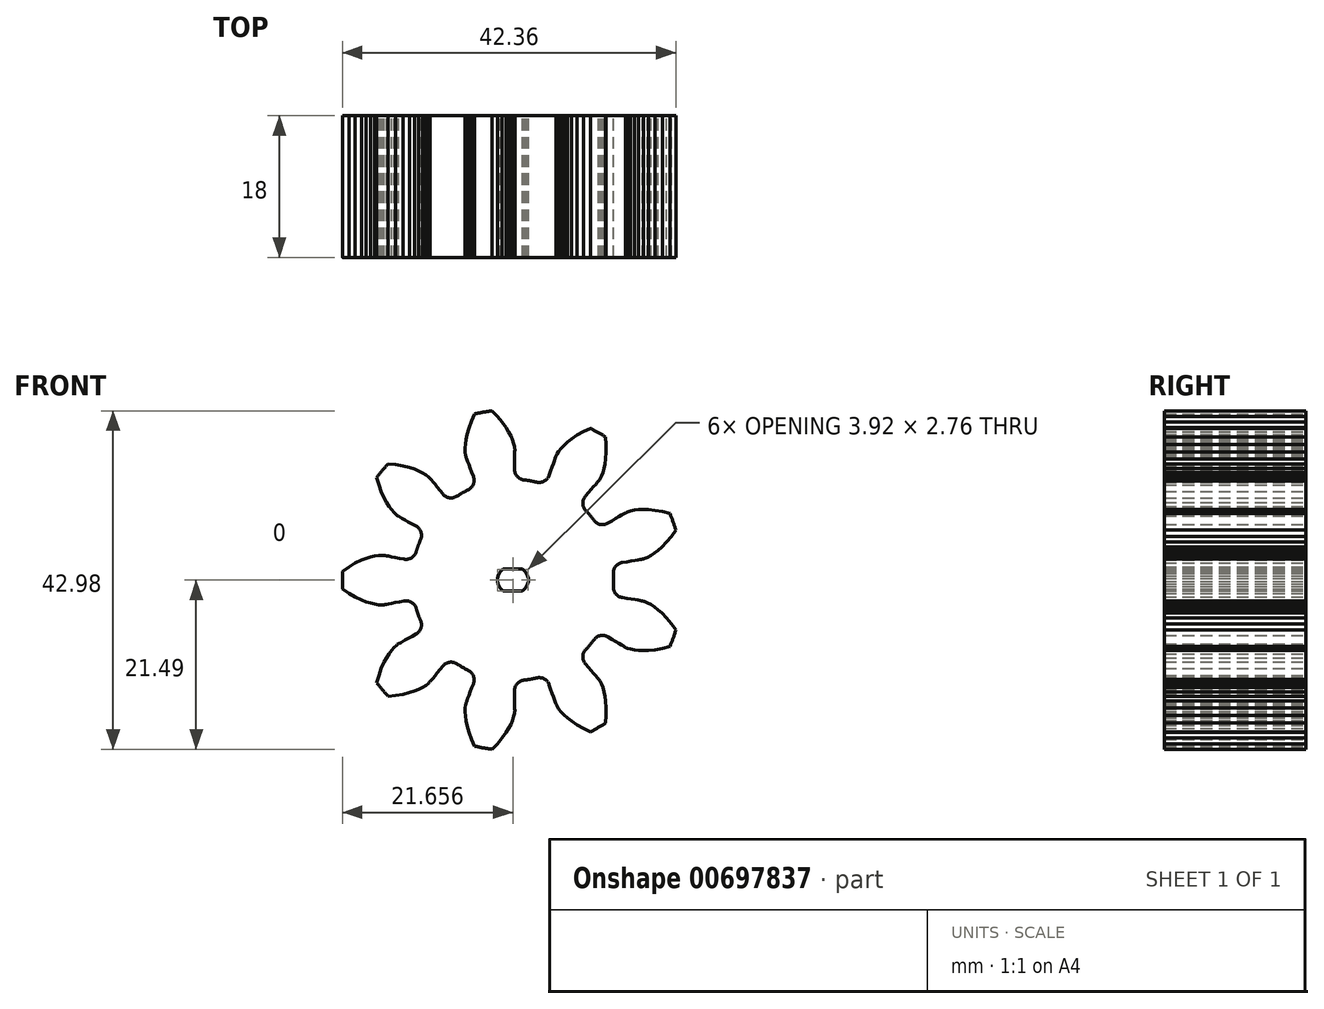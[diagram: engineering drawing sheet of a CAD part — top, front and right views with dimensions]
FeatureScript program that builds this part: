
annotation { "Feature Type Name" : "Feature", "Feature Type Description" : "" }
export const myFeature = defineFeature(function(context is Context, id is Id, definition is map)
    precondition{}
    {
        {
            var Q0;
            Q0=qCreatedBy(makeId("Front.planeOp"),FACE);
            var sketch = newSketch(context, id + "F0", { "sketchPlane" : qUnion([Q0])});
            skLineSegment(sketch, "E0", {"start": v(1.7, -1.38) * mm, "end": v(1.98, -1.13) * mm});
            skLineSegment(sketch, "E1", {"start": v(1.98, -1.13) * mm, "end": v(2.2, -0.84) * mm});
            skLineSegment(sketch, "E2", {"start": v(2.2, -0.84) * mm, "end": v(2.36, -0.52) * mm});
            skLineSegment(sketch, "E3", {"start": v(2.36, -0.52) * mm, "end": v(2.43, -0.18) * mm});
            skLineSegment(sketch, "E4", {"start": v(2.43, -0.18) * mm, "end": v(2.43, 0.18) * mm});
            skLineSegment(sketch, "E5", {"start": v(2.43, 0.18) * mm, "end": v(2.36, 0.52) * mm});
            skLineSegment(sketch, "E6", {"start": v(2.36, 0.52) * mm, "end": v(2.2, 0.84) * mm});
            skLineSegment(sketch, "E7", {"start": v(2.2, 0.84) * mm, "end": v(1.98, 1.13) * mm});
            skLineSegment(sketch, "E8", {"start": v(1.98, 1.13) * mm, "end": v(1.7, 1.38) * mm});
            skLineSegment(sketch, "E9", {"start": v(1.7, 1.38) * mm, "end": v(-0.75, 1.38) * mm});
            skLineSegment(sketch, "E10", {"start": v(-0.75, 1.38) * mm, "end": v(-1.03, 1.13) * mm});
            skLineSegment(sketch, "E11", {"start": v(-1.03, 1.13) * mm, "end": v(-1.25, 0.84) * mm});
            skLineSegment(sketch, "E12", {"start": v(-1.25, 0.84) * mm, "end": v(-1.4, 0.52) * mm});
            skLineSegment(sketch, "E13", {"start": v(-1.4, 0.52) * mm, "end": v(-1.48, 0.18) * mm});
            skLineSegment(sketch, "E14", {"start": v(-1.48, 0.18) * mm, "end": v(-1.48, -0.18) * mm});
            skLineSegment(sketch, "E15", {"start": v(-1.48, -0.18) * mm, "end": v(-1.4, -0.52) * mm});
            skLineSegment(sketch, "E16", {"start": v(-1.4, -0.52) * mm, "end": v(-1.25, -0.84) * mm});
            skLineSegment(sketch, "E17", {"start": v(-1.25, -0.84) * mm, "end": v(-1.03, -1.13) * mm});
            skLineSegment(sketch, "E18", {"start": v(-1.03, -1.13) * mm, "end": v(-0.75, -1.38) * mm});
            skLineSegment(sketch, "E19", {"start": v(1.7, -1.38) * mm, "end": v(-0.75, -1.38) * mm});
            skArc(sketch, "E20", {"start": v(20.42, -8.44) * mm, "mid": v(20.82, -7.4) * mm, "end": v(21.18, -6.35) * mm});
            skLineSegment(sketch, "E21", {"start": v(12.57, -7.23) * mm, "end": v(13.07, -7.53) * mm});
            skLineSegment(sketch, "E22", {"start": v(13.07, -7.53) * mm, "end": v(13.53, -7.8) * mm});
            skLineSegment(sketch, "E23", {"start": v(13.53, -7.8) * mm, "end": v(13.95, -8.05) * mm});
            skLineSegment(sketch, "E24", {"start": v(13.95, -8.05) * mm, "end": v(14.3, -8.26) * mm});
            skLineSegment(sketch, "E25", {"start": v(14.3, -8.26) * mm, "end": v(14.51, -8.39) * mm});
            skLineSegment(sketch, "E26", {"start": v(14.51, -8.39) * mm, "end": v(14.68, -8.48) * mm});
            skLineSegment(sketch, "E27", {"start": v(14.68, -8.48) * mm, "end": v(14.78, -8.54) * mm});
            skLineSegment(sketch, "E28", {"start": v(14.78, -8.54) * mm, "end": v(14.83, -8.57) * mm});
            skLineSegment(sketch, "E29", {"start": v(14.83, -8.57) * mm, "end": v(14.92, -8.6) * mm});
            skLineSegment(sketch, "E30", {"start": v(14.92, -8.6) * mm, "end": v(15.04, -8.66) * mm});
            skLineSegment(sketch, "E31", {"start": v(15.04, -8.66) * mm, "end": v(15.44, -8.78) * mm});
            skLineSegment(sketch, "E32", {"start": v(15.44, -8.78) * mm, "end": v(15.92, -8.87) * mm});
            skLineSegment(sketch, "E33", {"start": v(15.92, -8.87) * mm, "end": v(16.46, -8.94) * mm});
            skLineSegment(sketch, "E34", {"start": v(16.46, -8.94) * mm, "end": v(17.05, -8.96) * mm});
            skLineSegment(sketch, "E35", {"start": v(17.05, -8.96) * mm, "end": v(17.68, -8.95) * mm});
            skLineSegment(sketch, "E36", {"start": v(17.68, -8.95) * mm, "end": v(18.55, -8.86) * mm});
            skLineSegment(sketch, "E37", {"start": v(18.55, -8.86) * mm, "end": v(19.47, -8.7) * mm});
            skLineSegment(sketch, "E38", {"start": v(19.47, -8.7) * mm, "end": v(20.42, -8.44) * mm});
            skArc(sketch, "E39", {"start": v(10.78, -7.59) * mm, "mid": v(11.6, -7.06) * mm, "end": v(12.57, -7.23) * mm});
            skArc(sketch, "E40", {"start": v(9.74, -8.83) * mm, "mid": v(10.28, -8.22) * mm, "end": v(10.78, -7.59) * mm});
            skArc(sketch, "E41", {"start": v(9.7, -10.65) * mm, "mid": v(9.36, -9.73) * mm, "end": v(9.74, -8.83) * mm});
            skLineSegment(sketch, "E42", {"start": v(9.7, -10.65) * mm, "end": v(10.08, -11.1) * mm});
            skLineSegment(sketch, "E43", {"start": v(10.08, -11.1) * mm, "end": v(10.43, -11.5) * mm});
            skLineSegment(sketch, "E44", {"start": v(10.43, -11.5) * mm, "end": v(10.75, -11.87) * mm});
            skLineSegment(sketch, "E45", {"start": v(10.75, -11.87) * mm, "end": v(11, -12.17) * mm});
            skLineSegment(sketch, "E46", {"start": v(11, -12.17) * mm, "end": v(11.17, -12.36) * mm});
            skLineSegment(sketch, "E47", {"start": v(11.17, -12.36) * mm, "end": v(11.3, -12.51) * mm});
            skLineSegment(sketch, "E48", {"start": v(11.3, -12.51) * mm, "end": v(11.37, -12.6) * mm});
            skLineSegment(sketch, "E49", {"start": v(11.37, -12.6) * mm, "end": v(11.4, -12.64) * mm});
            skLineSegment(sketch, "E50", {"start": v(11.4, -12.64) * mm, "end": v(11.46, -12.73) * mm});
            skLineSegment(sketch, "E51", {"start": v(11.46, -12.73) * mm, "end": v(11.53, -12.84) * mm});
            skLineSegment(sketch, "E52", {"start": v(11.53, -12.84) * mm, "end": v(11.72, -13.21) * mm});
            skLineSegment(sketch, "E53", {"start": v(11.72, -13.21) * mm, "end": v(11.9, -13.66) * mm});
            skLineSegment(sketch, "E54", {"start": v(11.9, -13.66) * mm, "end": v(12.05, -14.19) * mm});
            skLineSegment(sketch, "E55", {"start": v(12.05, -14.19) * mm, "end": v(12.18, -14.76) * mm});
            skLineSegment(sketch, "E56", {"start": v(12.18, -14.76) * mm, "end": v(12.28, -15.38) * mm});
            skLineSegment(sketch, "E57", {"start": v(12.28, -15.38) * mm, "end": v(12.34, -16.26) * mm});
            skLineSegment(sketch, "E58", {"start": v(12.34, -16.26) * mm, "end": v(12.33, -17.2) * mm});
            skLineSegment(sketch, "E59", {"start": v(12.33, -17.2) * mm, "end": v(12.25, -18.17) * mm});
            skArc(sketch, "E60", {"start": v(10.32, -19.28) * mm, "mid": v(11.3, -18.75) * mm, "end": v(12.25, -18.17) * mm});
            skLineSegment(sketch, "E61", {"start": v(5.1, -13.31) * mm, "end": v(5.29, -13.86) * mm});
            skLineSegment(sketch, "E62", {"start": v(5.29, -13.86) * mm, "end": v(5.46, -14.37) * mm});
            skLineSegment(sketch, "E63", {"start": v(5.46, -14.37) * mm, "end": v(5.62, -14.83) * mm});
            skLineSegment(sketch, "E64", {"start": v(5.62, -14.83) * mm, "end": v(5.75, -15.2) * mm});
            skLineSegment(sketch, "E65", {"start": v(5.75, -15.2) * mm, "end": v(5.84, -15.45) * mm});
            skLineSegment(sketch, "E66", {"start": v(5.84, -15.45) * mm, "end": v(5.9, -15.63) * mm});
            skLineSegment(sketch, "E67", {"start": v(5.9, -15.63) * mm, "end": v(5.94, -15.74) * mm});
            skLineSegment(sketch, "E68", {"start": v(5.94, -15.74) * mm, "end": v(5.96, -15.79) * mm});
            skLineSegment(sketch, "E69", {"start": v(5.96, -15.79) * mm, "end": v(6, -15.88) * mm});
            skLineSegment(sketch, "E70", {"start": v(6, -15.88) * mm, "end": v(6.07, -16) * mm});
            skLineSegment(sketch, "E71", {"start": v(6.07, -16) * mm, "end": v(6.3, -16.34) * mm});
            skLineSegment(sketch, "E72", {"start": v(6.3, -16.34) * mm, "end": v(6.6, -16.72) * mm});
            skLineSegment(sketch, "E73", {"start": v(6.6, -16.72) * mm, "end": v(6.97, -17.12) * mm});
            skLineSegment(sketch, "E74", {"start": v(6.97, -17.12) * mm, "end": v(7.4, -17.52) * mm});
            skLineSegment(sketch, "E75", {"start": v(7.4, -17.52) * mm, "end": v(7.9, -17.91) * mm});
            skLineSegment(sketch, "E76", {"start": v(7.9, -17.91) * mm, "end": v(8.63, -18.4) * mm});
            skLineSegment(sketch, "E77", {"start": v(8.63, -18.4) * mm, "end": v(9.44, -18.87) * mm});
            skLineSegment(sketch, "E78", {"start": v(9.44, -18.87) * mm, "end": v(10.32, -19.28) * mm});
            skArc(sketch, "E79", {"start": v(3.5, -12.43) * mm, "mid": v(4.46, -12.56) * mm, "end": v(5.1, -13.31) * mm});
            skArc(sketch, "E80", {"start": v(1.9, -12.72) * mm, "mid": v(2.7, -12.6) * mm, "end": v(3.5, -12.43) * mm});
            skArc(sketch, "E81", {"start": v(0.69, -14.09) * mm, "mid": v(1.03, -13.17) * mm, "end": v(1.9, -12.72) * mm});
            skLineSegment(sketch, "E82", {"start": v(0.69, -14.09) * mm, "end": v(0.7, -14.67) * mm});
            skLineSegment(sketch, "E83", {"start": v(0.7, -14.67) * mm, "end": v(0.7, -15.21) * mm});
            skLineSegment(sketch, "E84", {"start": v(0.7, -15.21) * mm, "end": v(0.71, -15.7) * mm});
            skLineSegment(sketch, "E85", {"start": v(0.71, -15.7) * mm, "end": v(0.72, -16.1) * mm});
            skLineSegment(sketch, "E86", {"start": v(0.72, -16.1) * mm, "end": v(0.72, -16.35) * mm});
            skLineSegment(sketch, "E87", {"start": v(0.72, -16.35) * mm, "end": v(0.72, -16.54) * mm});
            skLineSegment(sketch, "E88", {"start": v(0.72, -16.54) * mm, "end": v(0.72, -16.66) * mm});
            skLineSegment(sketch, "E89", {"start": v(0.72, -16.66) * mm, "end": v(0.72, -16.71) * mm});
            skLineSegment(sketch, "E90", {"start": v(0.72, -16.71) * mm, "end": v(0.71, -16.81) * mm});
            skLineSegment(sketch, "E91", {"start": v(0.71, -16.81) * mm, "end": v(0.7, -16.95) * mm});
            skLineSegment(sketch, "E92", {"start": v(0.7, -16.95) * mm, "end": v(0.6, -17.35) * mm});
            skLineSegment(sketch, "E93", {"start": v(0.6, -17.35) * mm, "end": v(0.44, -17.8) * mm});
            skLineSegment(sketch, "E94", {"start": v(0.44, -17.8) * mm, "end": v(0.23, -18.3) * mm});
            skLineSegment(sketch, "E95", {"start": v(0.23, -18.3) * mm, "end": v(-0.05, -18.83) * mm});
            skLineSegment(sketch, "E96", {"start": v(-0.05, -18.83) * mm, "end": v(-0.37, -19.37) * mm});
            skLineSegment(sketch, "E97", {"start": v(-0.37, -19.37) * mm, "end": v(-0.89, -20.08) * mm});
            skLineSegment(sketch, "E98", {"start": v(-0.89, -20.08) * mm, "end": v(-1.5, -20.8) * mm});
            skLineSegment(sketch, "E99", {"start": v(-1.5, -20.8) * mm, "end": v(-2.18, -21.49) * mm});
            skArc(sketch, "E100", {"start": v(-4.37, -21.1) * mm, "mid": v(-3.28, -21.32) * mm, "end": v(-2.18, -21.49) * mm});
            skLineSegment(sketch, "E101", {"start": v(-4.54, -13.16) * mm, "end": v(-4.75, -13.71) * mm});
            skLineSegment(sketch, "E102", {"start": v(-4.75, -13.71) * mm, "end": v(-4.94, -14.22) * mm});
            skLineSegment(sketch, "E103", {"start": v(-4.94, -14.22) * mm, "end": v(-5.11, -14.66) * mm});
            skLineSegment(sketch, "E104", {"start": v(-5.11, -14.66) * mm, "end": v(-5.26, -15.04) * mm});
            skLineSegment(sketch, "E105", {"start": v(-5.26, -15.04) * mm, "end": v(-5.35, -15.28) * mm});
            skLineSegment(sketch, "E106", {"start": v(-5.35, -15.28) * mm, "end": v(-5.41, -15.46) * mm});
            skLineSegment(sketch, "E107", {"start": v(-5.41, -15.46) * mm, "end": v(-5.45, -15.57) * mm});
            skLineSegment(sketch, "E108", {"start": v(-5.45, -15.57) * mm, "end": v(-5.47, -15.62) * mm});
            skLineSegment(sketch, "E109", {"start": v(-5.47, -15.62) * mm, "end": v(-5.5, -15.72) * mm});
            skLineSegment(sketch, "E110", {"start": v(-5.5, -15.72) * mm, "end": v(-5.52, -15.85) * mm});
            skLineSegment(sketch, "E111", {"start": v(-5.52, -15.85) * mm, "end": v(-5.57, -16.26) * mm});
            skLineSegment(sketch, "E112", {"start": v(-5.57, -16.26) * mm, "end": v(-5.58, -16.75) * mm});
            skLineSegment(sketch, "E113", {"start": v(-5.58, -16.75) * mm, "end": v(-5.55, -17.29) * mm});
            skLineSegment(sketch, "E114", {"start": v(-5.55, -17.29) * mm, "end": v(-5.48, -17.87) * mm});
            skLineSegment(sketch, "E115", {"start": v(-5.48, -17.87) * mm, "end": v(-5.35, -18.5) * mm});
            skLineSegment(sketch, "E116", {"start": v(-5.35, -18.5) * mm, "end": v(-5.11, -19.34) * mm});
            skLineSegment(sketch, "E117", {"start": v(-5.11, -19.34) * mm, "end": v(-4.79, -20.21) * mm});
            skLineSegment(sketch, "E118", {"start": v(-4.79, -20.21) * mm, "end": v(-4.37, -21.1) * mm});
            skArc(sketch, "E119", {"start": v(-5.2, -11.46) * mm, "mid": v(-4.55, -12.19) * mm, "end": v(-4.54, -13.16) * mm});
            skArc(sketch, "E120", {"start": v(-6.61, -10.65) * mm, "mid": v(-5.92, -11.08) * mm, "end": v(-5.2, -11.46) * mm});
            skArc(sketch, "E121", {"start": v(-8.42, -10.93) * mm, "mid": v(-7.57, -10.44) * mm, "end": v(-6.61, -10.65) * mm});
            skLineSegment(sketch, "E122", {"start": v(-8.42, -10.93) * mm, "end": v(-8.78, -11.38) * mm});
            skLineSegment(sketch, "E123", {"start": v(-8.78, -11.38) * mm, "end": v(-9.12, -11.8) * mm});
            skLineSegment(sketch, "E124", {"start": v(-9.12, -11.8) * mm, "end": v(-9.43, -12.17) * mm});
            skLineSegment(sketch, "E125", {"start": v(-9.43, -12.17) * mm, "end": v(-9.68, -12.49) * mm});
            skLineSegment(sketch, "E126", {"start": v(-9.68, -12.49) * mm, "end": v(-9.84, -12.68) * mm});
            skLineSegment(sketch, "E127", {"start": v(-9.84, -12.68) * mm, "end": v(-9.96, -12.83) * mm});
            skLineSegment(sketch, "E128", {"start": v(-9.96, -12.83) * mm, "end": v(-10.04, -12.92) * mm});
            skLineSegment(sketch, "E129", {"start": v(-10.04, -12.92) * mm, "end": v(-10.08, -12.96) * mm});
            skLineSegment(sketch, "E130", {"start": v(-10.08, -12.96) * mm, "end": v(-10.15, -13.03) * mm});
            skLineSegment(sketch, "E131", {"start": v(-10.15, -13.03) * mm, "end": v(-10.25, -13.12) * mm});
            skLineSegment(sketch, "E132", {"start": v(-10.25, -13.12) * mm, "end": v(-10.58, -13.37) * mm});
            skLineSegment(sketch, "E133", {"start": v(-10.58, -13.37) * mm, "end": v(-11, -13.62) * mm});
            skLineSegment(sketch, "E134", {"start": v(-11, -13.62) * mm, "end": v(-11.48, -13.87) * mm});
            skLineSegment(sketch, "E135", {"start": v(-11.48, -13.87) * mm, "end": v(-12.03, -14.1) * mm});
            skLineSegment(sketch, "E136", {"start": v(-12.03, -14.1) * mm, "end": v(-12.63, -14.3) * mm});
            skLineSegment(sketch, "E137", {"start": v(-12.63, -14.3) * mm, "end": v(-13.48, -14.5) * mm});
            skLineSegment(sketch, "E138", {"start": v(-13.48, -14.5) * mm, "end": v(-14.4, -14.66) * mm});
            skLineSegment(sketch, "E139", {"start": v(-14.4, -14.66) * mm, "end": v(-15.37, -14.75) * mm});
            skArc(sketch, "E140", {"start": v(-16.8, -13.05) * mm, "mid": v(-16.11, -13.92) * mm, "end": v(-15.37, -14.75) * mm});
            skLineSegment(sketch, "E141", {"start": v(-11.83, -6.86) * mm, "end": v(-12.34, -7.14) * mm});
            skLineSegment(sketch, "E142", {"start": v(-12.34, -7.14) * mm, "end": v(-12.81, -7.4) * mm});
            skLineSegment(sketch, "E143", {"start": v(-12.81, -7.4) * mm, "end": v(-13.23, -7.64) * mm});
            skLineSegment(sketch, "E144", {"start": v(-13.23, -7.64) * mm, "end": v(-13.58, -7.84) * mm});
            skLineSegment(sketch, "E145", {"start": v(-13.58, -7.84) * mm, "end": v(-13.8, -7.96) * mm});
            skLineSegment(sketch, "E146", {"start": v(-13.8, -7.96) * mm, "end": v(-13.97, -8.05) * mm});
            skLineSegment(sketch, "E147", {"start": v(-13.97, -8.05) * mm, "end": v(-14.08, -8.11) * mm});
            skLineSegment(sketch, "E148", {"start": v(-14.08, -8.11) * mm, "end": v(-14.12, -8.14) * mm});
            skLineSegment(sketch, "E149", {"start": v(-14.12, -8.14) * mm, "end": v(-14.2, -8.2) * mm});
            skLineSegment(sketch, "E150", {"start": v(-14.2, -8.2) * mm, "end": v(-14.3, -8.29) * mm});
            skLineSegment(sketch, "E151", {"start": v(-14.3, -8.29) * mm, "end": v(-14.6, -8.57) * mm});
            skLineSegment(sketch, "E152", {"start": v(-14.6, -8.57) * mm, "end": v(-14.93, -8.93) * mm});
            skLineSegment(sketch, "E153", {"start": v(-14.93, -8.93) * mm, "end": v(-15.26, -9.37) * mm});
            skLineSegment(sketch, "E154", {"start": v(-15.26, -9.37) * mm, "end": v(-15.57, -9.87) * mm});
            skLineSegment(sketch, "E155", {"start": v(-15.57, -9.87) * mm, "end": v(-15.87, -10.42) * mm});
            skLineSegment(sketch, "E156", {"start": v(-15.87, -10.42) * mm, "end": v(-16.23, -11.22) * mm});
            skLineSegment(sketch, "E157", {"start": v(-16.23, -11.22) * mm, "end": v(-16.55, -12.1) * mm});
            skLineSegment(sketch, "E158", {"start": v(-16.55, -12.1) * mm, "end": v(-16.8, -13.05) * mm});
            skArc(sketch, "E159", {"start": v(-11.25, -5.13) * mm, "mid": v(-11.2, -6.1) * mm, "end": v(-11.83, -6.86) * mm});
            skArc(sketch, "E160", {"start": v(-11.8, -3.6) * mm, "mid": v(-11.55, -4.38) * mm, "end": v(-11.25, -5.13) * mm});
            skArc(sketch, "E161", {"start": v(-13.36, -2.66) * mm, "mid": v(-12.4, -2.83) * mm, "end": v(-11.8, -3.6) * mm});
            skLineSegment(sketch, "E162", {"start": v(-13.36, -2.66) * mm, "end": v(-13.93, -2.77) * mm});
            skLineSegment(sketch, "E163", {"start": v(-13.93, -2.77) * mm, "end": v(-14.46, -2.87) * mm});
            skLineSegment(sketch, "E164", {"start": v(-14.46, -2.87) * mm, "end": v(-14.94, -2.96) * mm});
            skLineSegment(sketch, "E165", {"start": v(-14.94, -2.96) * mm, "end": v(-15.33, -3.04) * mm});
            skLineSegment(sketch, "E166", {"start": v(-15.33, -3.04) * mm, "end": v(-15.58, -3.08) * mm});
            skLineSegment(sketch, "E167", {"start": v(-15.58, -3.08) * mm, "end": v(-15.77, -3.12) * mm});
            skLineSegment(sketch, "E168", {"start": v(-15.77, -3.12) * mm, "end": v(-15.89, -3.14) * mm});
            skLineSegment(sketch, "E169", {"start": v(-15.89, -3.14) * mm, "end": v(-15.94, -3.14) * mm});
            skLineSegment(sketch, "E170", {"start": v(-15.94, -3.14) * mm, "end": v(-16.04, -3.15) * mm});
            skLineSegment(sketch, "E171", {"start": v(-16.04, -3.15) * mm, "end": v(-16.17, -3.15) * mm});
            skLineSegment(sketch, "E172", {"start": v(-16.17, -3.15) * mm, "end": v(-16.59, -3.13) * mm});
            skLineSegment(sketch, "E173", {"start": v(-16.59, -3.13) * mm, "end": v(-17.07, -3.06) * mm});
            skLineSegment(sketch, "E174", {"start": v(-17.07, -3.06) * mm, "end": v(-17.6, -2.93) * mm});
            skLineSegment(sketch, "E175", {"start": v(-17.6, -2.93) * mm, "end": v(-18.16, -2.76) * mm});
            skLineSegment(sketch, "E176", {"start": v(-18.16, -2.76) * mm, "end": v(-18.75, -2.53) * mm});
            skLineSegment(sketch, "E177", {"start": v(-18.75, -2.53) * mm, "end": v(-19.54, -2.14) * mm});
            skLineSegment(sketch, "E178", {"start": v(-19.54, -2.14) * mm, "end": v(-20.34, -1.67) * mm});
            skLineSegment(sketch, "E179", {"start": v(-20.34, -1.67) * mm, "end": v(-21.15, -1.11) * mm});
            skArc(sketch, "E180", {"start": v(-21.15, 1.11) * mm, "mid": v(-21.18, 0) * mm, "end": v(-21.15, -1.11) * mm});
            skLineSegment(sketch, "E181", {"start": v(-13.36, 2.66) * mm, "end": v(-13.93, 2.77) * mm});
            skLineSegment(sketch, "E182", {"start": v(-13.93, 2.77) * mm, "end": v(-14.46, 2.87) * mm});
            skLineSegment(sketch, "E183", {"start": v(-14.46, 2.87) * mm, "end": v(-14.94, 2.96) * mm});
            skLineSegment(sketch, "E184", {"start": v(-14.94, 2.96) * mm, "end": v(-15.33, 3.04) * mm});
            skLineSegment(sketch, "E185", {"start": v(-15.33, 3.04) * mm, "end": v(-15.58, 3.08) * mm});
            skLineSegment(sketch, "E186", {"start": v(-15.58, 3.08) * mm, "end": v(-15.77, 3.12) * mm});
            skLineSegment(sketch, "E187", {"start": v(-15.77, 3.12) * mm, "end": v(-15.89, 3.14) * mm});
            skLineSegment(sketch, "E188", {"start": v(-15.89, 3.14) * mm, "end": v(-15.94, 3.14) * mm});
            skLineSegment(sketch, "E189", {"start": v(-15.94, 3.14) * mm, "end": v(-16.04, 3.15) * mm});
            skLineSegment(sketch, "E190", {"start": v(-16.04, 3.15) * mm, "end": v(-16.17, 3.15) * mm});
            skLineSegment(sketch, "E191", {"start": v(-16.17, 3.15) * mm, "end": v(-16.59, 3.13) * mm});
            skLineSegment(sketch, "E192", {"start": v(-16.59, 3.13) * mm, "end": v(-17.07, 3.06) * mm});
            skLineSegment(sketch, "E193", {"start": v(-17.07, 3.06) * mm, "end": v(-17.6, 2.93) * mm});
            skLineSegment(sketch, "E194", {"start": v(-17.6, 2.93) * mm, "end": v(-18.16, 2.76) * mm});
            skLineSegment(sketch, "E195", {"start": v(-18.16, 2.76) * mm, "end": v(-18.75, 2.53) * mm});
            skLineSegment(sketch, "E196", {"start": v(-18.75, 2.53) * mm, "end": v(-19.54, 2.14) * mm});
            skLineSegment(sketch, "E197", {"start": v(-19.54, 2.14) * mm, "end": v(-20.34, 1.67) * mm});
            skLineSegment(sketch, "E198", {"start": v(-20.34, 1.67) * mm, "end": v(-21.15, 1.11) * mm});
            skArc(sketch, "E199", {"start": v(-11.8, 3.6) * mm, "mid": v(-12.4, 2.83) * mm, "end": v(-13.36, 2.66) * mm});
            skArc(sketch, "E200", {"start": v(-11.25, 5.13) * mm, "mid": v(-11.55, 4.38) * mm, "end": v(-11.8, 3.6) * mm});
            skArc(sketch, "E201", {"start": v(-11.83, 6.86) * mm, "mid": v(-11.2, 6.1) * mm, "end": v(-11.25, 5.13) * mm});
            skLineSegment(sketch, "E202", {"start": v(-11.83, 6.86) * mm, "end": v(-12.34, 7.14) * mm});
            skLineSegment(sketch, "E203", {"start": v(-12.34, 7.14) * mm, "end": v(-12.81, 7.4) * mm});
            skLineSegment(sketch, "E204", {"start": v(-12.81, 7.4) * mm, "end": v(-13.23, 7.64) * mm});
            skLineSegment(sketch, "E205", {"start": v(-13.23, 7.64) * mm, "end": v(-13.58, 7.84) * mm});
            skLineSegment(sketch, "E206", {"start": v(-13.58, 7.84) * mm, "end": v(-13.8, 7.96) * mm});
            skLineSegment(sketch, "E207", {"start": v(-13.8, 7.96) * mm, "end": v(-13.97, 8.05) * mm});
            skLineSegment(sketch, "E208", {"start": v(-13.97, 8.05) * mm, "end": v(-14.08, 8.11) * mm});
            skLineSegment(sketch, "E209", {"start": v(-14.08, 8.11) * mm, "end": v(-14.12, 8.14) * mm});
            skLineSegment(sketch, "E210", {"start": v(-14.12, 8.14) * mm, "end": v(-14.2, 8.2) * mm});
            skLineSegment(sketch, "E211", {"start": v(-14.2, 8.2) * mm, "end": v(-14.3, 8.29) * mm});
            skLineSegment(sketch, "E212", {"start": v(-14.3, 8.29) * mm, "end": v(-14.6, 8.57) * mm});
            skLineSegment(sketch, "E213", {"start": v(-14.6, 8.57) * mm, "end": v(-14.93, 8.93) * mm});
            skLineSegment(sketch, "E214", {"start": v(-14.93, 8.93) * mm, "end": v(-15.26, 9.37) * mm});
            skLineSegment(sketch, "E215", {"start": v(-15.26, 9.37) * mm, "end": v(-15.57, 9.87) * mm});
            skLineSegment(sketch, "E216", {"start": v(-15.57, 9.87) * mm, "end": v(-15.87, 10.42) * mm});
            skLineSegment(sketch, "E217", {"start": v(-15.87, 10.42) * mm, "end": v(-16.23, 11.22) * mm});
            skLineSegment(sketch, "E218", {"start": v(-16.23, 11.22) * mm, "end": v(-16.55, 12.1) * mm});
            skLineSegment(sketch, "E219", {"start": v(-16.55, 12.1) * mm, "end": v(-16.8, 13.05) * mm});
            skArc(sketch, "E220", {"start": v(-15.37, 14.75) * mm, "mid": v(-16.11, 13.92) * mm, "end": v(-16.8, 13.05) * mm});
            skLineSegment(sketch, "E221", {"start": v(-8.42, 10.93) * mm, "end": v(-8.78, 11.38) * mm});
            skLineSegment(sketch, "E222", {"start": v(-8.78, 11.38) * mm, "end": v(-9.12, 11.8) * mm});
            skLineSegment(sketch, "E223", {"start": v(-9.12, 11.8) * mm, "end": v(-9.43, 12.17) * mm});
            skLineSegment(sketch, "E224", {"start": v(-9.43, 12.17) * mm, "end": v(-9.68, 12.49) * mm});
            skLineSegment(sketch, "E225", {"start": v(-9.68, 12.49) * mm, "end": v(-9.84, 12.68) * mm});
            skLineSegment(sketch, "E226", {"start": v(-9.84, 12.68) * mm, "end": v(-9.96, 12.83) * mm});
            skLineSegment(sketch, "E227", {"start": v(-9.96, 12.83) * mm, "end": v(-10.04, 12.92) * mm});
            skLineSegment(sketch, "E228", {"start": v(-10.04, 12.92) * mm, "end": v(-10.08, 12.96) * mm});
            skLineSegment(sketch, "E229", {"start": v(-10.08, 12.96) * mm, "end": v(-10.15, 13.03) * mm});
            skLineSegment(sketch, "E230", {"start": v(-10.15, 13.03) * mm, "end": v(-10.25, 13.12) * mm});
            skLineSegment(sketch, "E231", {"start": v(-10.25, 13.12) * mm, "end": v(-10.58, 13.37) * mm});
            skLineSegment(sketch, "E232", {"start": v(-10.58, 13.37) * mm, "end": v(-11, 13.62) * mm});
            skLineSegment(sketch, "E233", {"start": v(-11, 13.62) * mm, "end": v(-11.48, 13.87) * mm});
            skLineSegment(sketch, "E234", {"start": v(-11.48, 13.87) * mm, "end": v(-12.03, 14.1) * mm});
            skLineSegment(sketch, "E235", {"start": v(-12.03, 14.1) * mm, "end": v(-12.63, 14.3) * mm});
            skLineSegment(sketch, "E236", {"start": v(-12.63, 14.3) * mm, "end": v(-13.48, 14.5) * mm});
            skLineSegment(sketch, "E237", {"start": v(-13.48, 14.5) * mm, "end": v(-14.4, 14.66) * mm});
            skLineSegment(sketch, "E238", {"start": v(-14.4, 14.66) * mm, "end": v(-15.37, 14.75) * mm});
            skArc(sketch, "E239", {"start": v(-6.61, 10.65) * mm, "mid": v(-7.57, 10.44) * mm, "end": v(-8.42, 10.93) * mm});
            skArc(sketch, "E240", {"start": v(-5.2, 11.46) * mm, "mid": v(-5.92, 11.08) * mm, "end": v(-6.61, 10.65) * mm});
            skArc(sketch, "E241", {"start": v(-4.54, 13.16) * mm, "mid": v(-4.55, 12.19) * mm, "end": v(-5.2, 11.46) * mm});
            skLineSegment(sketch, "E242", {"start": v(-4.54, 13.16) * mm, "end": v(-4.75, 13.71) * mm});
            skLineSegment(sketch, "E243", {"start": v(-4.75, 13.71) * mm, "end": v(-4.94, 14.22) * mm});
            skLineSegment(sketch, "E244", {"start": v(-4.94, 14.22) * mm, "end": v(-5.11, 14.66) * mm});
            skLineSegment(sketch, "E245", {"start": v(-5.11, 14.66) * mm, "end": v(-5.26, 15.04) * mm});
            skLineSegment(sketch, "E246", {"start": v(-5.26, 15.04) * mm, "end": v(-5.35, 15.28) * mm});
            skLineSegment(sketch, "E247", {"start": v(-5.35, 15.28) * mm, "end": v(-5.41, 15.46) * mm});
            skLineSegment(sketch, "E248", {"start": v(-5.41, 15.46) * mm, "end": v(-5.45, 15.57) * mm});
            skLineSegment(sketch, "E249", {"start": v(-5.45, 15.57) * mm, "end": v(-5.47, 15.62) * mm});
            skLineSegment(sketch, "E250", {"start": v(-5.47, 15.62) * mm, "end": v(-5.5, 15.72) * mm});
            skLineSegment(sketch, "E251", {"start": v(-5.5, 15.72) * mm, "end": v(-5.52, 15.85) * mm});
            skLineSegment(sketch, "E252", {"start": v(-5.52, 15.85) * mm, "end": v(-5.57, 16.26) * mm});
            skLineSegment(sketch, "E253", {"start": v(-5.57, 16.26) * mm, "end": v(-5.58, 16.75) * mm});
            skLineSegment(sketch, "E254", {"start": v(-5.58, 16.75) * mm, "end": v(-5.55, 17.29) * mm});
            skLineSegment(sketch, "E255", {"start": v(-5.55, 17.29) * mm, "end": v(-5.48, 17.87) * mm});
            skLineSegment(sketch, "E256", {"start": v(-5.48, 17.87) * mm, "end": v(-5.35, 18.5) * mm});
            skLineSegment(sketch, "E257", {"start": v(-5.35, 18.5) * mm, "end": v(-5.11, 19.34) * mm});
            skLineSegment(sketch, "E258", {"start": v(-5.11, 19.34) * mm, "end": v(-4.79, 20.21) * mm});
            skLineSegment(sketch, "E259", {"start": v(-4.79, 20.21) * mm, "end": v(-4.37, 21.1) * mm});
            skArc(sketch, "E260", {"start": v(-2.18, 21.49) * mm, "mid": v(-3.28, 21.32) * mm, "end": v(-4.37, 21.1) * mm});
            skLineSegment(sketch, "E261", {"start": v(0.69, 14.09) * mm, "end": v(0.7, 14.67) * mm});
            skLineSegment(sketch, "E262", {"start": v(0.7, 14.67) * mm, "end": v(0.7, 15.21) * mm});
            skLineSegment(sketch, "E263", {"start": v(0.7, 15.21) * mm, "end": v(0.71, 15.7) * mm});
            skLineSegment(sketch, "E264", {"start": v(0.71, 15.7) * mm, "end": v(0.72, 16.1) * mm});
            skLineSegment(sketch, "E265", {"start": v(0.72, 16.1) * mm, "end": v(0.72, 16.35) * mm});
            skLineSegment(sketch, "E266", {"start": v(0.72, 16.35) * mm, "end": v(0.72, 16.54) * mm});
            skLineSegment(sketch, "E267", {"start": v(0.72, 16.54) * mm, "end": v(0.72, 16.66) * mm});
            skLineSegment(sketch, "E268", {"start": v(0.72, 16.66) * mm, "end": v(0.72, 16.71) * mm});
            skLineSegment(sketch, "E269", {"start": v(0.72, 16.71) * mm, "end": v(0.71, 16.81) * mm});
            skLineSegment(sketch, "E270", {"start": v(0.71, 16.81) * mm, "end": v(0.7, 16.95) * mm});
            skLineSegment(sketch, "E271", {"start": v(0.7, 16.95) * mm, "end": v(0.6, 17.35) * mm});
            skLineSegment(sketch, "E272", {"start": v(0.6, 17.35) * mm, "end": v(0.44, 17.8) * mm});
            skLineSegment(sketch, "E273", {"start": v(0.44, 17.8) * mm, "end": v(0.23, 18.3) * mm});
            skLineSegment(sketch, "E274", {"start": v(0.23, 18.3) * mm, "end": v(-0.05, 18.83) * mm});
            skLineSegment(sketch, "E275", {"start": v(-0.05, 18.83) * mm, "end": v(-0.37, 19.37) * mm});
            skLineSegment(sketch, "E276", {"start": v(-0.37, 19.37) * mm, "end": v(-0.89, 20.08) * mm});
            skLineSegment(sketch, "E277", {"start": v(-0.89, 20.08) * mm, "end": v(-1.5, 20.8) * mm});
            skLineSegment(sketch, "E278", {"start": v(-1.5, 20.8) * mm, "end": v(-2.18, 21.49) * mm});
            skArc(sketch, "E279", {"start": v(1.9, 12.72) * mm, "mid": v(1.03, 13.17) * mm, "end": v(0.69, 14.09) * mm});
            skArc(sketch, "E280", {"start": v(3.5, 12.43) * mm, "mid": v(2.7, 12.6) * mm, "end": v(1.9, 12.72) * mm});
            skArc(sketch, "E281", {"start": v(5.1, 13.31) * mm, "mid": v(4.46, 12.56) * mm, "end": v(3.5, 12.43) * mm});
            skLineSegment(sketch, "E282", {"start": v(5.1, 13.31) * mm, "end": v(5.29, 13.86) * mm});
            skLineSegment(sketch, "E283", {"start": v(5.29, 13.86) * mm, "end": v(5.46, 14.37) * mm});
            skLineSegment(sketch, "E284", {"start": v(5.46, 14.37) * mm, "end": v(5.62, 14.83) * mm});
            skLineSegment(sketch, "E285", {"start": v(5.62, 14.83) * mm, "end": v(5.75, 15.2) * mm});
            skLineSegment(sketch, "E286", {"start": v(5.75, 15.2) * mm, "end": v(5.84, 15.45) * mm});
            skLineSegment(sketch, "E287", {"start": v(5.84, 15.45) * mm, "end": v(5.9, 15.63) * mm});
            skLineSegment(sketch, "E288", {"start": v(5.9, 15.63) * mm, "end": v(5.94, 15.74) * mm});
            skLineSegment(sketch, "E289", {"start": v(5.94, 15.74) * mm, "end": v(5.96, 15.79) * mm});
            skLineSegment(sketch, "E290", {"start": v(5.96, 15.79) * mm, "end": v(6, 15.88) * mm});
            skLineSegment(sketch, "E291", {"start": v(6, 15.88) * mm, "end": v(6.07, 16) * mm});
            skLineSegment(sketch, "E292", {"start": v(6.07, 16) * mm, "end": v(6.3, 16.34) * mm});
            skLineSegment(sketch, "E293", {"start": v(6.3, 16.34) * mm, "end": v(6.6, 16.72) * mm});
            skLineSegment(sketch, "E294", {"start": v(6.6, 16.72) * mm, "end": v(6.97, 17.12) * mm});
            skLineSegment(sketch, "E295", {"start": v(6.97, 17.12) * mm, "end": v(7.4, 17.52) * mm});
            skLineSegment(sketch, "E296", {"start": v(7.4, 17.52) * mm, "end": v(7.9, 17.91) * mm});
            skLineSegment(sketch, "E297", {"start": v(7.9, 17.91) * mm, "end": v(8.63, 18.4) * mm});
            skLineSegment(sketch, "E298", {"start": v(8.63, 18.4) * mm, "end": v(9.44, 18.87) * mm});
            skLineSegment(sketch, "E299", {"start": v(9.44, 18.87) * mm, "end": v(10.32, 19.28) * mm});
            skArc(sketch, "E300", {"start": v(12.25, 18.17) * mm, "mid": v(11.3, 18.75) * mm, "end": v(10.32, 19.28) * mm});
            skLineSegment(sketch, "E301", {"start": v(9.7, 10.65) * mm, "end": v(10.08, 11.1) * mm});
            skLineSegment(sketch, "E302", {"start": v(10.08, 11.1) * mm, "end": v(10.43, 11.5) * mm});
            skLineSegment(sketch, "E303", {"start": v(10.43, 11.5) * mm, "end": v(10.75, 11.87) * mm});
            skLineSegment(sketch, "E304", {"start": v(10.75, 11.87) * mm, "end": v(11, 12.17) * mm});
            skLineSegment(sketch, "E305", {"start": v(11, 12.17) * mm, "end": v(11.17, 12.36) * mm});
            skLineSegment(sketch, "E306", {"start": v(11.17, 12.36) * mm, "end": v(11.3, 12.51) * mm});
            skLineSegment(sketch, "E307", {"start": v(11.3, 12.51) * mm, "end": v(11.37, 12.6) * mm});
            skLineSegment(sketch, "E308", {"start": v(11.37, 12.6) * mm, "end": v(11.4, 12.64) * mm});
            skLineSegment(sketch, "E309", {"start": v(11.4, 12.64) * mm, "end": v(11.46, 12.73) * mm});
            skLineSegment(sketch, "E310", {"start": v(11.46, 12.73) * mm, "end": v(11.53, 12.84) * mm});
            skLineSegment(sketch, "E311", {"start": v(11.53, 12.84) * mm, "end": v(11.72, 13.21) * mm});
            skLineSegment(sketch, "E312", {"start": v(11.72, 13.21) * mm, "end": v(11.9, 13.66) * mm});
            skLineSegment(sketch, "E313", {"start": v(11.9, 13.66) * mm, "end": v(12.05, 14.19) * mm});
            skLineSegment(sketch, "E314", {"start": v(12.05, 14.19) * mm, "end": v(12.18, 14.76) * mm});
            skLineSegment(sketch, "E315", {"start": v(12.18, 14.76) * mm, "end": v(12.28, 15.38) * mm});
            skLineSegment(sketch, "E316", {"start": v(12.28, 15.38) * mm, "end": v(12.34, 16.26) * mm});
            skLineSegment(sketch, "E317", {"start": v(12.34, 16.26) * mm, "end": v(12.33, 17.2) * mm});
            skLineSegment(sketch, "E318", {"start": v(12.33, 17.2) * mm, "end": v(12.25, 18.17) * mm});
            skArc(sketch, "E319", {"start": v(9.74, 8.83) * mm, "mid": v(9.36, 9.73) * mm, "end": v(9.7, 10.65) * mm});
            skArc(sketch, "E320", {"start": v(10.78, 7.59) * mm, "mid": v(10.28, 8.22) * mm, "end": v(9.74, 8.83) * mm});
            skArc(sketch, "E321", {"start": v(12.57, 7.23) * mm, "mid": v(11.6, 7.06) * mm, "end": v(10.78, 7.59) * mm});
            skLineSegment(sketch, "E322", {"start": v(12.57, 7.23) * mm, "end": v(13.07, 7.53) * mm});
            skLineSegment(sketch, "E323", {"start": v(13.07, 7.53) * mm, "end": v(13.53, 7.8) * mm});
            skLineSegment(sketch, "E324", {"start": v(13.53, 7.8) * mm, "end": v(13.95, 8.05) * mm});
            skLineSegment(sketch, "E325", {"start": v(13.95, 8.05) * mm, "end": v(14.3, 8.26) * mm});
            skLineSegment(sketch, "E326", {"start": v(14.3, 8.26) * mm, "end": v(14.51, 8.39) * mm});
            skLineSegment(sketch, "E327", {"start": v(14.51, 8.39) * mm, "end": v(14.68, 8.48) * mm});
            skLineSegment(sketch, "E328", {"start": v(14.68, 8.48) * mm, "end": v(14.78, 8.54) * mm});
            skLineSegment(sketch, "E329", {"start": v(14.78, 8.54) * mm, "end": v(14.83, 8.57) * mm});
            skLineSegment(sketch, "E330", {"start": v(14.83, 8.57) * mm, "end": v(14.92, 8.6) * mm});
            skLineSegment(sketch, "E331", {"start": v(14.92, 8.6) * mm, "end": v(15.04, 8.66) * mm});
            skLineSegment(sketch, "E332", {"start": v(15.04, 8.66) * mm, "end": v(15.44, 8.78) * mm});
            skLineSegment(sketch, "E333", {"start": v(15.44, 8.78) * mm, "end": v(15.92, 8.87) * mm});
            skLineSegment(sketch, "E334", {"start": v(15.92, 8.87) * mm, "end": v(16.46, 8.94) * mm});
            skLineSegment(sketch, "E335", {"start": v(16.46, 8.94) * mm, "end": v(17.05, 8.96) * mm});
            skLineSegment(sketch, "E336", {"start": v(17.05, 8.96) * mm, "end": v(17.68, 8.95) * mm});
            skLineSegment(sketch, "E337", {"start": v(17.68, 8.95) * mm, "end": v(18.55, 8.86) * mm});
            skLineSegment(sketch, "E338", {"start": v(18.55, 8.86) * mm, "end": v(19.47, 8.7) * mm});
            skLineSegment(sketch, "E339", {"start": v(19.47, 8.7) * mm, "end": v(20.42, 8.44) * mm});
            skArc(sketch, "E340", {"start": v(21.18, 6.35) * mm, "mid": v(20.82, 7.4) * mm, "end": v(20.42, 8.44) * mm});
            skLineSegment(sketch, "E341", {"start": v(14.39, 2.24) * mm, "end": v(14.96, 2.33) * mm});
            skLineSegment(sketch, "E342", {"start": v(14.96, 2.33) * mm, "end": v(15.5, 2.41) * mm});
            skLineSegment(sketch, "E343", {"start": v(15.5, 2.41) * mm, "end": v(15.97, 2.49) * mm});
            skLineSegment(sketch, "E344", {"start": v(15.97, 2.49) * mm, "end": v(16.37, 2.55) * mm});
            skLineSegment(sketch, "E345", {"start": v(16.37, 2.55) * mm, "end": v(16.62, 2.6) * mm});
            skLineSegment(sketch, "E346", {"start": v(16.62, 2.6) * mm, "end": v(16.8, 2.63) * mm});
            skLineSegment(sketch, "E347", {"start": v(16.8, 2.63) * mm, "end": v(16.93, 2.65) * mm});
            skLineSegment(sketch, "E348", {"start": v(16.93, 2.65) * mm, "end": v(16.98, 2.66) * mm});
            skLineSegment(sketch, "E349", {"start": v(16.98, 2.66) * mm, "end": v(17.07, 2.69) * mm});
            skLineSegment(sketch, "E350", {"start": v(17.07, 2.69) * mm, "end": v(17.2, 2.73) * mm});
            skLineSegment(sketch, "E351", {"start": v(17.2, 2.73) * mm, "end": v(17.58, 2.9) * mm});
            skLineSegment(sketch, "E352", {"start": v(17.58, 2.9) * mm, "end": v(18, 3.13) * mm});
            skLineSegment(sketch, "E353", {"start": v(18, 3.13) * mm, "end": v(18.46, 3.42) * mm});
            skLineSegment(sketch, "E354", {"start": v(18.46, 3.42) * mm, "end": v(18.93, 3.78) * mm});
            skLineSegment(sketch, "E355", {"start": v(18.93, 3.78) * mm, "end": v(19.4, 4.2) * mm});
            skLineSegment(sketch, "E356", {"start": v(19.4, 4.2) * mm, "end": v(20.02, 4.83) * mm});
            skLineSegment(sketch, "E357", {"start": v(20.02, 4.83) * mm, "end": v(20.61, 5.55) * mm});
            skLineSegment(sketch, "E358", {"start": v(20.61, 5.55) * mm, "end": v(21.18, 6.35) * mm});
            skArc(sketch, "E359", {"start": v(13.25, 0.81) * mm, "mid": v(13.54, 1.74) * mm, "end": v(14.39, 2.24) * mm});
            skArc(sketch, "E360", {"start": v(13.25, -0.81) * mm, "mid": v(13.27, 0) * mm, "end": v(13.25, 0.81) * mm});
            skArc(sketch, "E361", {"start": v(14.39, -2.24) * mm, "mid": v(13.54, -1.74) * mm, "end": v(13.25, -0.81) * mm});
            skLineSegment(sketch, "E362", {"start": v(14.39, -2.24) * mm, "end": v(14.96, -2.33) * mm});
            skLineSegment(sketch, "E363", {"start": v(14.96, -2.33) * mm, "end": v(15.5, -2.41) * mm});
            skLineSegment(sketch, "E364", {"start": v(15.5, -2.41) * mm, "end": v(15.97, -2.49) * mm});
            skLineSegment(sketch, "E365", {"start": v(15.97, -2.49) * mm, "end": v(16.37, -2.55) * mm});
            skLineSegment(sketch, "E366", {"start": v(16.37, -2.55) * mm, "end": v(16.62, -2.6) * mm});
            skLineSegment(sketch, "E367", {"start": v(16.62, -2.6) * mm, "end": v(16.8, -2.63) * mm});
            skLineSegment(sketch, "E368", {"start": v(16.8, -2.63) * mm, "end": v(16.93, -2.65) * mm});
            skLineSegment(sketch, "E369", {"start": v(16.93, -2.65) * mm, "end": v(16.98, -2.66) * mm});
            skLineSegment(sketch, "E370", {"start": v(16.98, -2.66) * mm, "end": v(17.07, -2.69) * mm});
            skLineSegment(sketch, "E371", {"start": v(17.07, -2.69) * mm, "end": v(17.2, -2.73) * mm});
            skLineSegment(sketch, "E372", {"start": v(17.2, -2.73) * mm, "end": v(17.58, -2.9) * mm});
            skLineSegment(sketch, "E373", {"start": v(17.58, -2.9) * mm, "end": v(18, -3.13) * mm});
            skLineSegment(sketch, "E374", {"start": v(18, -3.13) * mm, "end": v(18.46, -3.42) * mm});
            skLineSegment(sketch, "E375", {"start": v(18.46, -3.42) * mm, "end": v(18.93, -3.78) * mm});
            skLineSegment(sketch, "E376", {"start": v(18.93, -3.78) * mm, "end": v(19.4, -4.2) * mm});
            skLineSegment(sketch, "E377", {"start": v(19.4, -4.2) * mm, "end": v(20.02, -4.83) * mm});
            skLineSegment(sketch, "E378", {"start": v(20.02, -4.83) * mm, "end": v(20.61, -5.55) * mm});
            skLineSegment(sketch, "E379", {"start": v(20.61, -5.55) * mm, "end": v(21.18, -6.35) * mm});
            skSolve(sketch);
        }
        {
            var Q0;
            Q0 = qSketchRegion(id + "F0", true);
            extrude(context, id + "F1", {"entities" : qUnion([Q0]), "depth" : 18 * mm, "offsetDistance" : 25 * mm});
        }
    });
